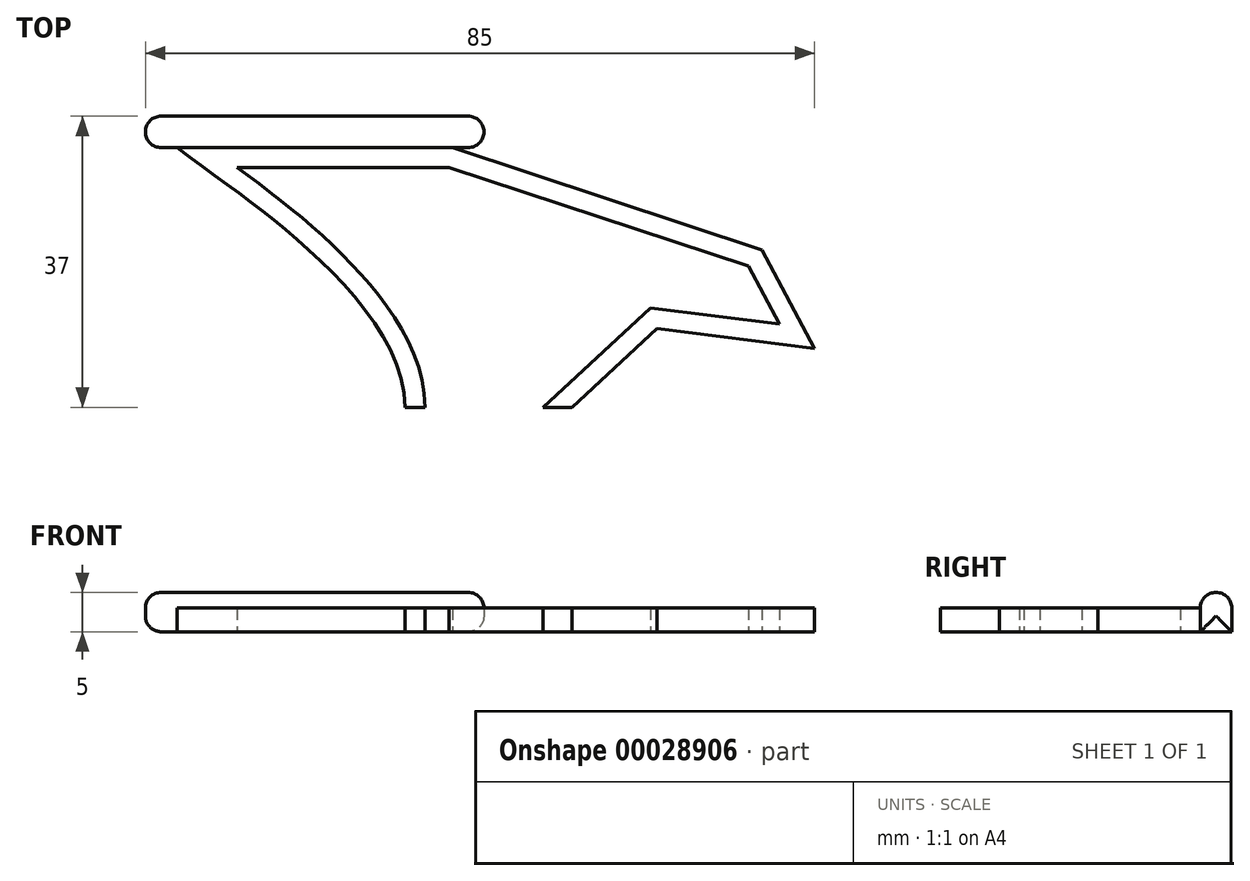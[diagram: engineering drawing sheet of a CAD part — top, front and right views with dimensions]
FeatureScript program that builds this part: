
annotation { "Feature Type Name" : "Feature", "Feature Type Description" : "" }
export const myFeature = defineFeature(function(context is Context, id is Id, definition is map)
    precondition{}
    {
        {
            var Q0;
            Q0=qCreatedBy(makeId("Top.planeOp"),FACE);
            var sketch = newSketch(context, id + "F0", { "sketchPlane" : qUnion([Q0])});
            skLineSegment(sketch, "E0", {"start": v(0, 0) * mm, "end": v(52, 0) * mm});
            skLineSegment(sketch, "E1", {"start": v(52, 0) * mm, "end": v(52, 7.5) * mm, "construction": true});
            skLineSegment(sketch, "E2", {"start": v(32, 0) * mm, "end": v(32, 10) * mm, "construction": true});
            skPoint(sketch, "E3", {"position": v(21.21, 0) * mm});
            skLineSegment(sketch, "E4", {"start": v(6, 0) * mm, "end": v(6, 33) * mm, "construction": true});
            skLineSegment(sketch, "E5", {"start": v(6, 33) * mm, "end": v(-29, 33) * mm});
            skLineSegment(sketch, "E6", {"start": v(52, 7.5) * mm, "end": v(32, 10) * mm});
            skLineSegment(sketch, "E7", {"start": v(32, 10) * mm, "end": v(21.21, 0) * mm});
            skLineSegment(sketch, "E8", {"start": v(52, 7.5) * mm, "end": v(45.32, 20) * mm});
            skLineSegment(sketch, "E9", {"start": v(45.32, 20) * mm, "end": v(6, 33) * mm});
            skFitSpline(sketch, "E10", {"points": [v(-29, 33) * mm, v(-11.62, 19.43) * mm, v(0, 0) * mm], "startDerivative": vector(38.2, -28.49) * mm, "endDerivative": vector(0, -42.4) * mm});
            skFitSpline(sketch, "E11.MirrorCS", {"points": [v(-29, -33) * mm, v(-11.62, -19.43) * mm, v(0, 0) * mm], "startDerivative": vector(38.2, 28.49) * mm, "endDerivative": vector(0, 42.4) * mm});
            skLineSegment(sketch, "E12.MirrorCS", {"start": v(45.32, -20) * mm, "end": v(6, -33) * mm});
            skLineSegment(sketch, "E13.MirrorCS", {"start": v(32, 0) * mm, "end": v(32, -10) * mm, "construction": true});
            skLineSegment(sketch, "E14.MirrorCS", {"start": v(52, -7.5) * mm, "end": v(45.32, -20) * mm});
            skLineSegment(sketch, "E15.MirrorCS", {"start": v(52, -7.5) * mm, "end": v(32, -10) * mm});
            skLineSegment(sketch, "E16.MirrorCS", {"start": v(52, 0) * mm, "end": v(52, -7.5) * mm, "construction": true});
            skLineSegment(sketch, "E17.MirrorCS", {"start": v(32, -10) * mm, "end": v(21.21, 0) * mm});
            skLineSegment(sketch, "E18.MirrorCS", {"start": v(6, 0) * mm, "end": v(6, -33) * mm, "construction": true});
            skLineSegment(sketch, "E19.MirrorCS", {"start": v(6, -33) * mm, "end": v(-29, -33) * mm});
            skLineSegment(sketch, "E20.bottom", {"start": v(-33, 33) * mm, "end": v(10, 33) * mm});
            skLineSegment(sketch, "E20.top", {"start": v(-33, 37) * mm, "end": v(10, 37) * mm});
            skLineSegment(sketch, "E20.left", {"start": v(-33, 33) * mm, "end": v(-33, 37) * mm});
            skLineSegment(sketch, "E20.right", {"start": v(10, 33) * mm, "end": v(10, 37) * mm});
            skLineSegment(sketch, "E21.MirrorCS", {"start": v(10, -33) * mm, "end": v(10, -37) * mm});
            skLineSegment(sketch, "E22.MirrorCS", {"start": v(-33, -33) * mm, "end": v(-33, -37) * mm});
            skLineSegment(sketch, "E23.MirrorCS", {"start": v(-33, -33) * mm, "end": v(10, -33) * mm});
            skLineSegment(sketch, "E24.MirrorCS", {"start": v(-33, -37) * mm, "end": v(10, -37) * mm});
            skSolve(sketch);
        }
        {
            var Q0;
            Q0=makeQuery(id+"F0.imprint","IMPRINT",FACE,{"disambiguationData":[TD([[makeQuery(id+"F0.imprint","IMPRINT",EDGE,{"derivedFrom":sQuery(id+"F0.wireOp",EDGE,"E6")}),-1.0]])]});
            var Q1;
            {var subQ1=sQuery(id+"F0.wireOp",EDGE,"E11.MirrorCS");Q1=makeQuery(id+"F0.imprint","IMPRINT",FACE,{"disambiguationData":[TD([[makeQuery(id+"F0.imprint","IMPRINT",EDGE,{"derivedFrom":subQ1}),-1.0]])]});}
            var Q2;
            Q2=sQuery(id+"F0.wireOp",EDGE,"E18.MirrorCS");
            extrude(context, id + "F1", {"entities" : qUnion([Q0, Q1]), "surfaceEntities" : qUnion([Q2]), "depth" : 3 * mm});
        }
        {
            var Q0;
            Q0=makeQuery(id+"F1.opExtrude","CAP_FACE",FACE,{"disambiguationData":[OSD([sQuery(id+"F0.wireOp",EDGE,"E6"),sQuery(id+"F0.wireOp",EDGE,"E7"),sQuery(id+"F0.wireOp",EDGE,"E8"),sQuery(id+"F0.wireOp",EDGE,"E9"),sQuery(id+"F0.wireOp",EDGE,"E10"),sQuery(id+"F0.wireOp",EDGE,"E11.MirrorCS"),sQuery(id+"F0.wireOp",EDGE,"E12.MirrorCS"),sQuery(id+"F0.wireOp",EDGE,"E14.MirrorCS"),sQuery(id+"F0.wireOp",EDGE,"E15.MirrorCS"),sQuery(id+"F0.wireOp",EDGE,"E17.MirrorCS"),sQuery(id+"F0.wireOp",EDGE,"E20.bottom"),sQuery(id+"F0.wireOp",EDGE,"E19.MirrorCS")])],"isStart":false});
            var Q1;
            Q1=makeQuery(id+"F1.opExtrude","CAP_FACE",FACE,{"disambiguationData":[OSD([sQuery(id+"F0.wireOp",EDGE,"E6"),sQuery(id+"F0.wireOp",EDGE,"E7"),sQuery(id+"F0.wireOp",EDGE,"E8"),sQuery(id+"F0.wireOp",EDGE,"E9"),sQuery(id+"F0.wireOp",EDGE,"E10"),sQuery(id+"F0.wireOp",EDGE,"E11.MirrorCS"),sQuery(id+"F0.wireOp",EDGE,"E12.MirrorCS"),sQuery(id+"F0.wireOp",EDGE,"E14.MirrorCS"),sQuery(id+"F0.wireOp",EDGE,"E15.MirrorCS"),sQuery(id+"F0.wireOp",EDGE,"E17.MirrorCS"),sQuery(id+"F0.wireOp",EDGE,"E20.bottom"),sQuery(id+"F0.wireOp",EDGE,"E19.MirrorCS")])],"isStart":true});
            shell(context, id + "F2", {"entities" : qUnion([Q0, Q1]), "thickness" : 2.5 * mm});
        }
        {
            var Q0;
            Q0=makeQuery(id+"F0.imprint","IMPRINT",FACE,{"disambiguationData":[TD([[makeQuery(id+"F0.imprint","IMPRINT",EDGE,{"derivedFrom":sQuery(id+"F0.wireOp",EDGE,"E20.top")}),-1.0]])]});
            var Q1;
            {var subQ2=sQuery(id+"F0.wireOp",EDGE,"E21.MirrorCS");Q1=makeQuery(id+"F0.imprint","IMPRINT",FACE,{"disambiguationData":[TD([[makeQuery(id+"F0.imprint","IMPRINT",EDGE,{"derivedFrom":subQ2}),-1.0]])]});}
            extrude(context, id + "F3", {"entities" : qUnion([Q0, Q1]), "operationType" : NewBodyOperationType.ADD, "depth" : 5 * mm});
        }
        {
            var Q0;
            Q0=makeQuery(id+"F3.opExtrude","SWEPT_FACE",FACE,{"disambiguationData":[OSD([sQuery(id+"F0.wireOp",EDGE,"E20.right")])]});
            var Q1;
            Q1=makeQuery(id+"F3.opExtrude","SWEPT_FACE",FACE,{"disambiguationData":[OSD([sQuery(id+"F0.wireOp",EDGE,"E21.MirrorCS")])]});
            var Q2;
            Q2=makeQuery(id+"F3.opExtrude","SWEPT_FACE",FACE,{"disambiguationData":[OSD([sQuery(id+"F0.wireOp",EDGE,"E20.left")])]});
            var Q3;
            Q3=makeQuery(id+"F3.opExtrude","SWEPT_FACE",FACE,{"disambiguationData":[OSD([sQuery(id+"F0.wireOp",EDGE,"E22.MirrorCS")])]});
            var Q4;
            Q4=makeQuery(id+"F3.opExtrude","CAP_FACE",FACE,{"disambiguationData":[OSD([sQuery(id+"F0.wireOp",EDGE,"E20.bottom"),sQuery(id+"F0.wireOp",EDGE,"E20.top"),sQuery(id+"F0.wireOp",EDGE,"E20.left"),sQuery(id+"F0.wireOp",EDGE,"E20.right")])],"isStart":false});
            var Q5;
            Q5=makeQuery(id+"F3.opExtrude","CAP_FACE",FACE,{"disambiguationData":[OSD([sQuery(id+"F0.wireOp",EDGE,"E21.MirrorCS"),sQuery(id+"F0.wireOp",EDGE,"E22.MirrorCS"),sQuery(id+"F0.wireOp",EDGE,"E23.MirrorCS"),sQuery(id+"F0.wireOp",EDGE,"E24.MirrorCS"),sQuery(id+"F0.wireOp",EDGE,"E19.MirrorCS")])],"isStart":false});
            fillet(context, id + "F4", {"entities" : qUnion([Q0, Q1, Q2, Q3, Q4, Q5]), "radius" : 2 * mm, "tangentPropagation" : true, "allowEdgeOverflow" : false});
        }
        {
            var Q0;
            Q0=qCreatedBy(makeId("Top.planeOp"),FACE);
            var sketch = newSketch(context, id + "F5", { "sketchPlane" : qUnion([Q0])});
            skLineSegment(sketch, "E25.bottom", {"start": v(-68.1, 0) * mm, "end": v(90.54, 0) * mm});
            skLineSegment(sketch, "E25.top", {"start": v(-68.1, -59.13) * mm, "end": v(90.54, -59.13) * mm});
            skLineSegment(sketch, "E25.left", {"start": v(-68.1, 0) * mm, "end": v(-68.1, -59.13) * mm});
            skLineSegment(sketch, "E25.right", {"start": v(90.54, 0) * mm, "end": v(90.54, -59.13) * mm});
            skSolve(sketch);
        }
        {
            var Q0;
            Q0 = qSketchRegion(id + "F5", true);
            extrude(context, id + "F6", {"entities" : qUnion([Q0]), "operationType" : NewBodyOperationType.REMOVE, "depth" : 25 * mm});
        }
    });
